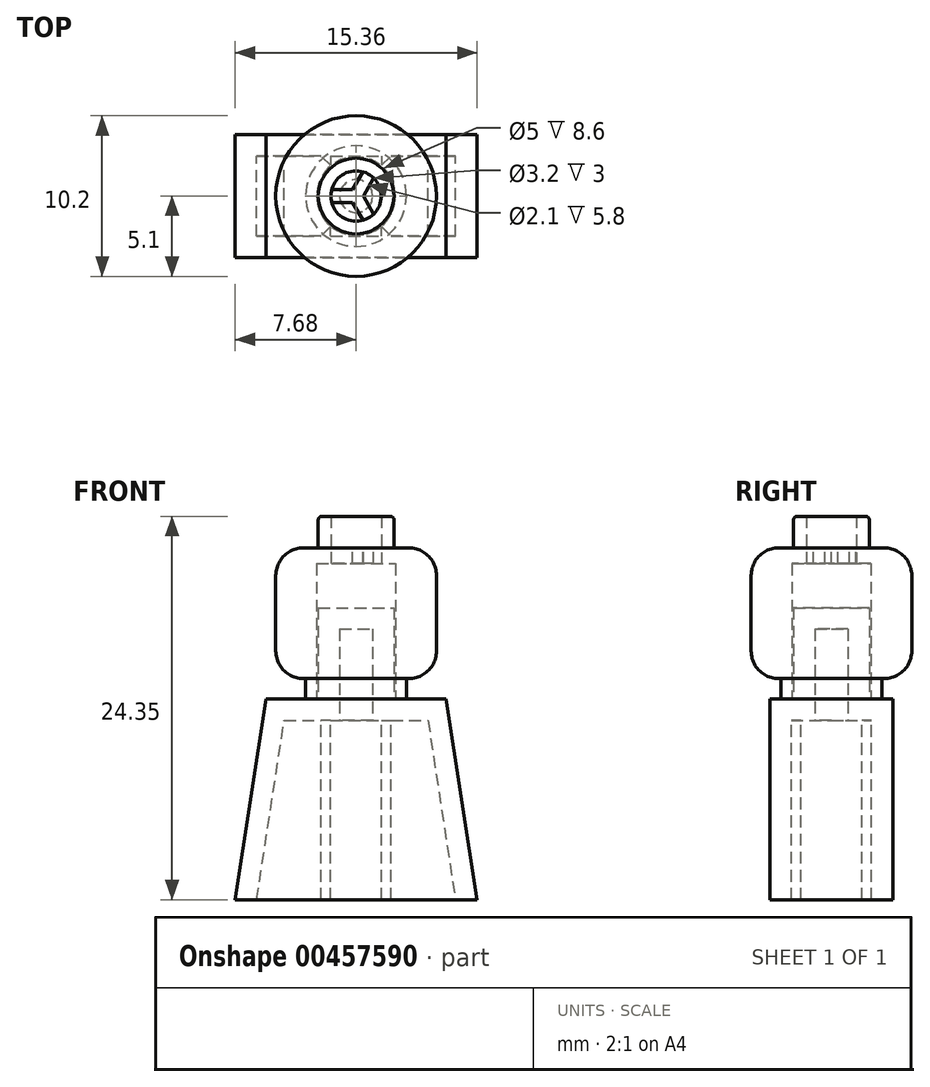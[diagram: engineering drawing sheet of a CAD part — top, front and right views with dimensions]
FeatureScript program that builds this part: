
annotation { "Feature Type Name" : "Feature", "Feature Type Description" : "" }
export const myFeature = defineFeature(function(context is Context, id is Id, definition is map)
    precondition{}
    {
        {
            var Q0;
            Q0=qCreatedBy(makeId("Front.planeOp"),FACE);
            var sketch = newSketch(context, id + "F0", { "sketchPlane" : qUnion([Q0])});
            skLineSegment(sketch, "E0", {"start": v(0, 0) * mm, "end": v(0, 11.6) * mm});
            skLineSegment(sketch, "E1", {"start": v(0, 0) * mm, "end": v(2.5, 0) * mm});
            skLineSegment(sketch, "E2", {"start": v(2.5, 0) * mm, "end": v(3.2, 0) * mm});
            skLineSegment(sketch, "E3", {"start": v(3.2, 0) * mm, "end": v(3.2, 1.3) * mm});
            skLineSegment(sketch, "E4", {"start": v(3.2, 1.3) * mm, "end": v(3.35, 1.3) * mm});
            skLineSegment(sketch, "E5", {"start": v(5.1, 3.05) * mm, "end": v(5.1, 7.85) * mm});
            skLineSegment(sketch, "E6", {"start": v(3.35, 9.6) * mm, "end": v(2.4, 9.6) * mm});
            skLineSegment(sketch, "E7", {"start": v(2.4, 9.6) * mm, "end": v(2.4, 11.4) * mm});
            skLineSegment(sketch, "E8", {"start": v(2.2, 11.6) * mm, "end": v(1.6, 11.6) * mm});
            skLineSegment(sketch, "E9", {"start": v(1.6, 11.6) * mm, "end": v(1.6, 9.6) * mm});
            skLineSegment(sketch, "E10", {"start": v(1.6, 9.6) * mm, "end": v(0, 9.6) * mm});
            skLineSegment(sketch, "E11", {"start": v(0, 9.6) * mm, "end": v(0, 8.6) * mm});
            skLineSegment(sketch, "E12", {"start": v(0, 8.6) * mm, "end": v(2.5, 8.6) * mm});
            skLineSegment(sketch, "E13", {"start": v(2.5, 8.6) * mm, "end": v(2.5, 0) * mm});
            skPoint(sketch, "E14.visualSharp", {"position": v(5.1, 9.6) * mm});
            skArc(sketch, "E14.filletArc", {"start": v(5.1, 7.85) * mm, "mid": v(4.59, 9.09) * mm, "end": v(3.35, 9.6) * mm});
            skPoint(sketch, "E15.visualSharp", {"position": v(5.1, 1.3) * mm});
            skArc(sketch, "E15.filletArc", {"start": v(3.35, 1.3) * mm, "mid": v(4.59, 1.81) * mm, "end": v(5.1, 3.05) * mm});
            skPoint(sketch, "E16.visualSharp", {"position": v(2.4, 11.6) * mm});
            skArc(sketch, "E16.filletArc", {"start": v(2.4, 11.4) * mm, "mid": v(2.34, 11.54) * mm, "end": v(2.2, 11.6) * mm});
            skSolve(sketch);
        }
        {
            var Q0;
            Q0=makeQuery(id+"F0.imprint","IMPRINT",FACE,{"disambiguationData":[TD([[makeQuery(id+"F0.imprint","IMPRINT",EDGE,{"derivedFrom":sQuery(id+"F0.wireOp",EDGE,"E2")}),1.0]])]});
            var Q1;
            Q1=sQuery(id+"F0.wireOp",EDGE,"E0");
            revolve(context, id + "F1", {"entities" : qUnion([Q0]), "axis" : qUnion([Q1]), "revolveType" : RevolveType.FULL});
        }
        {
            var Q0;
            Q0=makeQuery(id+"F1.opRevolve","SWEPT_FACE",FACE,{"disambiguationData":[OSD([sQuery(id+"F0.wireOp",EDGE,"E10")])]});
            var sketch = newSketch(context, id + "F2", { "sketchPlane" : qUnion([Q0])});
            skCircle(sketch, "E17", {"center": v(0, 0) * mm, "radius": 0.4 * mm});
            skLineSegment(sketch, "E18", {"start": v(0, 0.4) * mm, "end": v(0, -0.4) * mm});
            skLineSegment(sketch, "E19", {"start": v(0, -0.4) * mm, "end": v(-1.55, -0.4) * mm});
            skLineSegment(sketch, "E20", {"start": v(0, 0.4) * mm, "end": v(-1.55, 0.4) * mm});
            skLineSegment(sketch, "E21.1.0", {"start": v(-0.35, -0.2) * mm, "end": v(0.43, -1.54) * mm});
            skLineSegment(sketch, "E21.1.1", {"start": v(0.35, 0.2) * mm, "end": v(1.12, -1.14) * mm});
            skLineSegment(sketch, "E21.2.0", {"start": v(0.35, -0.2) * mm, "end": v(1.12, 1.14) * mm});
            skLineSegment(sketch, "E21.2.1", {"start": v(-0.35, 0.2) * mm, "end": v(0.43, 1.54) * mm});
            skSolve(sketch);
        }
        {
            var Q0;
            {var subQ0=sQuery(id+"F2.wireOp",EDGE,"E20");var subQ3=sQuery(id+"F2.wireOp",EDGE,"E21.2.1");var subQ4=makeQuery(id+"F2.imprint","INTERSECT",VERTEX,{"derivedFrom":[subQ0,subQ3]});Q0=makeQuery(id+"F2.imprint","IMPRINT",FACE,{"disambiguationData":[TD([[makeQuery(id+"F2.imprint","IMPRINT",EDGE,{"disambiguationData":[TD([[subQ4,-1.0]])],"derivedFrom":subQ0}),-1.0]])]});}
            var Q1;
            {var subQ0=sQuery(id+"F2.wireOp",EDGE,"E21.1.1");var subQ3=sQuery(id+"F2.wireOp",EDGE,"E21.2.0");var subQ4=makeQuery(id+"F2.imprint","INTERSECT",VERTEX,{"derivedFrom":[subQ0,subQ3]});Q1=makeQuery(id+"F2.imprint","IMPRINT",FACE,{"disambiguationData":[TD([[makeQuery(id+"F2.imprint","IMPRINT",EDGE,{"disambiguationData":[TD([[subQ4,-1.0]])],"derivedFrom":subQ0}),1.0]])]});}
            var Q2;
            {var subQ0=sQuery(id+"F2.wireOp",EDGE,"E19");var subQ3=sQuery(id+"F2.wireOp",EDGE,"E21.1.0");var subQ4=makeQuery(id+"F2.imprint","INTERSECT",VERTEX,{"derivedFrom":[subQ0,subQ3]});Q2=makeQuery(id+"F2.imprint","IMPRINT",FACE,{"disambiguationData":[TD([[makeQuery(id+"F2.imprint","IMPRINT",EDGE,{"disambiguationData":[TD([[subQ4,-1.0]])],"derivedFrom":subQ0}),1.0]])]});}
            extrude(context, id + "F3", {"entities" : qUnion([Q0, Q1, Q2]), "operationType" : NewBodyOperationType.REMOVE, "oppositeDirection" : true, "depth" : 25 * mm});
        }
        {
            var Q0;
            Q0=makeQuery(id+"F1.opRevolve","SWEPT_FACE",FACE,{"disambiguationData":[OSD([sQuery(id+"F0.wireOp",EDGE,"E2")])]});
            var sketch = newSketch(context, id + "F4", { "sketchPlane" : qUnion([Q0])});
            skCircle(sketch, "E22", {"center": v(0, 0) * mm, "radius": 2.4 * mm});
            skSolve(sketch);
        }
        {
            var Q0;
            Q0 = qSketchRegion(id + "F4", true);
            extrude(context, id + "F5", {"entities" : qUnion([Q0]), "oppositeDirection" : true, "depth" : 5.8 * mm});
        }
        {
            var Q0;
            Q0=qCreatedBy(makeId("Front.planeOp"),FACE);
            var sketch = newSketch(context, id + "F6", { "sketchPlane" : qUnion([Q0])});
            skLineSegment(sketch, "E23", {"start": v(0, 0) * mm, "end": v(0, -12.75) * mm, "construction": true});
            skLineSegment(sketch, "E24", {"start": v(0, 0) * mm, "end": v(-5.72, 0) * mm});
            skLineSegment(sketch, "E25", {"start": v(-5.72, 0) * mm, "end": v(5.72, 0) * mm});
            skLineSegment(sketch, "E26", {"start": v(5.72, 0) * mm, "end": v(7.67, -12.75) * mm});
            skLineSegment(sketch, "E27", {"start": v(7.67, -12.75) * mm, "end": v(-7.67, -12.75) * mm});
            skLineSegment(sketch, "E28", {"start": v(-7.67, -12.75) * mm, "end": v(-5.72, 0) * mm});
            skSolve(sketch);
        }
        {
            var Q0;
            {var subQ2=sQuery(id+"F6.wireOp",EDGE,"E26");Q0=makeQuery(id+"F6.imprint","IMPRINT",FACE,{"disambiguationData":[TD([[makeQuery(id+"F6.imprint","IMPRINT",EDGE,{"derivedFrom":subQ2}),-1.0]])]});}
            extrude(context, id + "F7", {"entities" : qUnion([Q0]), "operationType" : NewBodyOperationType.ADD, "endBound" : BoundingType.SYMMETRIC, "depth" : 7.8 * mm, "offsetDistance" : 25 * mm});
        }
        {
            var Q0;
            Q0=makeQuery(id+"F7.opExtrude","SWEPT_FACE",FACE,{"disambiguationData":[OSD([sQuery(id+"F6.wireOp",EDGE,"E27")])]});
            shell(context, id + "F8", {"entities" : qUnion([Q0]), "thickness" : 1.35 * mm});
        }
        {
            var Q0;
            Q0=makeQuery(id+"F8.opShell","OFFSET_FACE",FACE,{"disambiguationData":[OSD([sQuery(id+"F6.wireOp",EDGE,"E25")])]});
            var sketch = newSketch(context, id + "F9", { "sketchPlane" : qUnion([Q0])});
            skLineSegment(sketch, "E29", {"start": v(0, 2.55) * mm, "end": v(0, -2.55) * mm});
            skLineSegment(sketch, "E30", {"start": v(-1.63, 2.55) * mm, "end": v(-1.63, 1.95) * mm});
            skLineSegment(sketch, "E31", {"start": v(-1.63, 1.95) * mm, "end": v(-2.23, 2.55) * mm});
            skLineSegment(sketch, "E32", {"start": v(-4.57, 0) * mm, "end": v(4.57, 0) * mm});
            skLineSegment(sketch, "E33.MirrorCS", {"start": v(1.62, 1.95) * mm, "end": v(2.22, 2.55) * mm});
            skLineSegment(sketch, "E34.MirrorCS", {"start": v(1.62, 2.55) * mm, "end": v(1.62, 1.95) * mm});
            skLineSegment(sketch, "E35.MirrorCS", {"start": v(4.57, 0) * mm, "end": v(-4.57, 0) * mm});
            skLineSegment(sketch, "E36.MirrorCS", {"start": v(1.62, -1.95) * mm, "end": v(2.22, -2.55) * mm});
            skLineSegment(sketch, "E37.MirrorCS", {"start": v(-1.63, -1.95) * mm, "end": v(-2.23, -2.55) * mm});
            skLineSegment(sketch, "E38.MirrorCS", {"start": v(-1.63, -2.55) * mm, "end": v(-1.63, -1.95) * mm});
            skLineSegment(sketch, "E39.MirrorCS", {"start": v(1.62, -2.55) * mm, "end": v(1.62, -1.95) * mm});
            skSolve(sketch);
        }
        {
            var Q0;
            {var subQ0=sQuery(id+"F9.wireOp",EDGE,"E30");Q0=makeQuery(id+"F9.imprint","IMPRINT",FACE,{"disambiguationData":[TD([[makeQuery(id+"F9.imprint","IMPRINT",EDGE,{"derivedFrom":subQ0}),-1.0]])]});}
            var Q1;
            {var subQ0=sQuery(id+"F9.wireOp",EDGE,"E33.MirrorCS");Q1=makeQuery(id+"F9.imprint","IMPRINT",FACE,{"disambiguationData":[TD([[makeQuery(id+"F9.imprint","IMPRINT",EDGE,{"derivedFrom":subQ0}),1.0]])]});}
            var Q2;
            {var subQ0=sQuery(id+"F9.wireOp",EDGE,"E37.MirrorCS");Q2=makeQuery(id+"F9.imprint","IMPRINT",FACE,{"disambiguationData":[TD([[makeQuery(id+"F9.imprint","IMPRINT",EDGE,{"derivedFrom":subQ0}),1.0]])]});}
            var Q3;
            {var subQ0=sQuery(id+"F9.wireOp",EDGE,"E36.MirrorCS");Q3=makeQuery(id+"F9.imprint","IMPRINT",FACE,{"disambiguationData":[TD([[makeQuery(id+"F9.imprint","IMPRINT",EDGE,{"derivedFrom":subQ0}),-1.0]])]});}
            var Q4;
            Q4=makeQuery(id+"F7.opExtrude","SWEPT_FACE",FACE,{"disambiguationData":[OSD([sQuery(id+"F6.wireOp",EDGE,"E27")])]});
            extrude(context, id + "F10", {"entities" : qUnion([Q0, Q1, Q2, Q3]), "operationType" : NewBodyOperationType.ADD, "endBound" : BoundingType.UP_TO_SURFACE, "depth" : 25 * mm, "endBoundEntityFace" : qUnion([Q4]), "offsetDistance" : 25 * mm});
        }
    });
